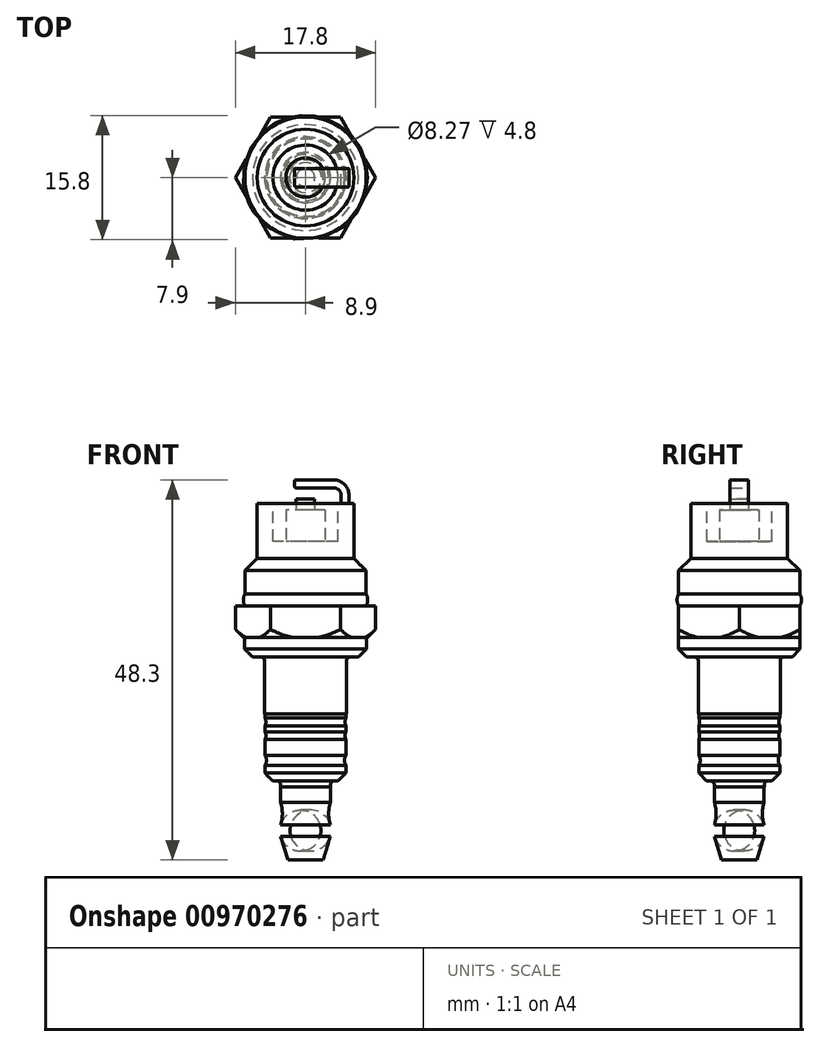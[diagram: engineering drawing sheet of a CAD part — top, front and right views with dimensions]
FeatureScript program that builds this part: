
annotation { "Feature Type Name" : "Feature", "Feature Type Description" : "" }
export const myFeature = defineFeature(function(context is Context, id is Id, definition is map)
    precondition{}
    {
        {
            var Q0;
            Q0=qCreatedBy(makeId("Front.planeOp"),FACE);
            var sketch = newSketch(context, id + "F0", { "sketchPlane" : qUnion([Q0])});
            skLineSegment(sketch, "E0", {"start": v(0, 22.65) * mm, "end": v(0, -22.65) * mm});
            skLineSegment(sketch, "E1", {"start": v(0, -22.65) * mm, "end": v(2.25, -22.65) * mm});
            skLineSegment(sketch, "E2", {"start": v(2.25, -22.65) * mm, "end": v(3.15, -19.65) * mm});
            skLineSegment(sketch, "E3", {"start": v(3.15, -18.15) * mm, "end": v(3.15, -15.35) * mm, "construction": true});
            skLineSegment(sketch, "E4", {"start": v(6.14, 22.65) * mm, "end": v(6.14, 15.65) * mm});
            skLineSegment(sketch, "E5", {"start": v(6.14, 15.65) * mm, "end": v(7.7, 14.15) * mm});
            skLineSegment(sketch, "E6", {"start": v(7.7, 14.15) * mm, "end": v(7.7, 11.15) * mm});
            skLineSegment(sketch, "E7", {"start": v(7.7, 11.15) * mm, "end": v(7.7, 9.65) * mm, "construction": true});
            skLineSegment(sketch, "E8", {"start": v(7.7, 9.65) * mm, "end": v(8.9, 9.65) * mm});
            skLineSegment(sketch, "E9", {"start": v(8.9, 9.65) * mm, "end": v(8.9, 5.65) * mm});
            skLineSegment(sketch, "E10", {"start": v(8.9, 5.65) * mm, "end": v(7.73, 5.65) * mm});
            skLineSegment(sketch, "E11", {"start": v(7.73, 5.65) * mm, "end": v(7.73, 3.15) * mm});
            skLineSegment(sketch, "E12", {"start": v(7.73, 3.15) * mm, "end": v(5.2, 3.15) * mm});
            skLineSegment(sketch, "E13", {"start": v(7.73, -1275.75) * mm, "end": v(7.53, -1275.75) * mm});
            skLineSegment(sketch, "E14", {"start": v(7.53, -408.95) * mm, "end": v(7.53, -1275.75) * mm});
            skLineSegment(sketch, "E15", {"start": v(7.53, -408.95) * mm, "end": v(7.73, -408.95) * mm});
            skLineSegment(sketch, "E16", {"start": v(7.73, -408.95) * mm, "end": v(7.73, -408.95) * mm});
            skLineSegment(sketch, "E17", {"start": v(5.2, -4.1) * mm, "end": v(5.15, -4.1) * mm});
            skLineSegment(sketch, "E18", {"start": v(5.15, -4.1) * mm, "end": v(5.15, -4.6) * mm});
            skLineSegment(sketch, "E19", {"start": v(5.15, -12.6) * mm, "end": v(3.18, -12.6) * mm});
            skLineSegment(sketch, "E20", {"start": v(3.18, -12.6) * mm, "end": v(3.18, -13.35) * mm});
            skLineSegment(sketch, "E21", {"start": v(3.18, -13.35) * mm, "end": v(3.15, -13.35) * mm});
            skLineSegment(sketch, "E22", {"start": v(3.15, -13.35) * mm, "end": v(3.15, -15.35) * mm});
            skLineSegment(sketch, "E23", {"start": v(6.14, 22.65) * mm, "end": v(4.14, 22.65) * mm});
            skLineSegment(sketch, "E24", {"start": v(4.14, 22.65) * mm, "end": v(4.14, 17.85) * mm});
            skLineSegment(sketch, "E25", {"start": v(4.14, 17.85) * mm, "end": v(0, 17.85) * mm});
            skArc(sketch, "E26", {"start": v(7.7, 9.65) * mm, "mid": v(7.9, 10.4) * mm, "end": v(7.7, 11.15) * mm});
            skPoint(sketch, "E27", {"position": v(3.15, -18.15) * mm});
            skArc(sketch, "E28", {"start": v(3.15, -19.65) * mm, "mid": v(3.26, -18.9) * mm, "end": v(3.15, -18.15) * mm});
            skArc(sketch, "E29", {"start": v(3.15, -15.35) * mm, "mid": v(2.94, -16.75) * mm, "end": v(3.15, -18.15) * mm});
            skLineSegment(sketch, "E30", {"start": v(5.2, -4.1) * mm, "end": v(5.2, 3.15) * mm});
            skLineSegment(sketch, "E31", {"start": v(5.15, -10.6) * mm, "end": v(5.15, -12.6) * mm});
            skLineSegment(sketch, "E32", {"start": v(5.15, -9.35) * mm, "end": v(5.15, -10.6) * mm, "construction": true});
            skLineSegment(sketch, "E33", {"start": v(5.15, -7.35) * mm, "end": v(5.15, -9.35) * mm});
            skLineSegment(sketch, "E34", {"start": v(5.15, -6.35) * mm, "end": v(5.15, -7.35) * mm, "construction": true});
            skLineSegment(sketch, "E35", {"start": v(5.15, -5.6) * mm, "end": v(5.15, -6.35) * mm});
            skLineSegment(sketch, "E36", {"start": v(5.15, -4.6) * mm, "end": v(5.15, -5.6) * mm, "construction": true});
            skArc(sketch, "E37", {"start": v(5.15, -9.35) * mm, "mid": v(4.96, -9.98) * mm, "end": v(5.15, -10.6) * mm});
            skArc(sketch, "E38", {"start": v(5.15, -4.6) * mm, "mid": v(5.03, -5.1) * mm, "end": v(5.15, -5.6) * mm});
            skArc(sketch, "E39", {"start": v(5.15, -6.35) * mm, "mid": v(5.03, -6.85) * mm, "end": v(5.15, -7.35) * mm});
            skSolve(sketch);
        }
        {
            var Q0;
            {var subQ1=sQuery(id+"F0.wireOp",EDGE,"E1");Q0=makeQuery(id+"F0.imprint","IMPRINT",FACE,{"disambiguationData":[TD([[makeQuery(id+"F0.imprint","IMPRINT",EDGE,{"derivedFrom":subQ1}),1.0]])]});}
            var Q1;
            Q1=sQuery(id+"F0.wireOp",EDGE,"E0");
            revolve(context, id + "F1", {"entities" : qUnion([Q0]), "axis" : qUnion([Q1]), "revolveType" : RevolveType.FULL});
        }
        {
            var Q0;
            Q0=makeQuery(id+"F1.opRevolve","SWEPT_FACE",FACE,{"disambiguationData":[OSD([sQuery(id+"F0.wireOp",EDGE,"E8")])]});
            var sketch = newSketch(context, id + "F2", { "sketchPlane" : qUnion([Q0])});
            skCircle(sketch, "E40.cCircle", {"center": v(0, 0) * mm, "radius": 7.7 * mm, "construction": true});
            skLineSegment(sketch, "E40.0", {"start": v(-4.45, 7.7) * mm, "end": v(4.45, 7.7) * mm});
            skLineSegment(sketch, "E40.1", {"start": v(4.45, 7.7) * mm, "end": v(8.9, 0) * mm});
            skLineSegment(sketch, "E40.2", {"start": v(8.9, 0) * mm, "end": v(4.45, -7.7) * mm});
            skLineSegment(sketch, "E40.3", {"start": v(4.45, -7.7) * mm, "end": v(-4.45, -7.7) * mm});
            skLineSegment(sketch, "E40.4", {"start": v(-4.45, -7.7) * mm, "end": v(-8.9, 0) * mm});
            skLineSegment(sketch, "E40.5", {"start": v(-8.9, 0) * mm, "end": v(-4.45, 7.7) * mm});
            skPoint(sketch, "E40.0.midPoint", {"position": v(0, 7.7) * mm});
            skSolve(sketch);
        }
        {
            var Q0;
            {var subQ0=sQuery(id+"F2.wireOp",EDGE,"E40.5");Q0=makeQuery(id+"F2.imprint","IMPRINT",FACE,{"disambiguationData":[TD([[makeQuery(id+"F2.imprint","IMPRINT",EDGE,{"derivedFrom":subQ0}),1.0]])]});}
            var Q1;
            {var subQ0=sQuery(id+"F2.wireOp",EDGE,"E40.4");Q1=makeQuery(id+"F2.imprint","IMPRINT",FACE,{"disambiguationData":[TD([[makeQuery(id+"F2.imprint","IMPRINT",EDGE,{"derivedFrom":subQ0}),1.0]])]});}
            var Q2;
            {var subQ0=sQuery(id+"F2.wireOp",EDGE,"E40.3");Q2=makeQuery(id+"F2.imprint","IMPRINT",FACE,{"disambiguationData":[TD([[makeQuery(id+"F2.imprint","IMPRINT",EDGE,{"derivedFrom":subQ0}),1.0]])]});}
            var Q3;
            {var subQ0=sQuery(id+"F2.wireOp",EDGE,"E40.2");Q3=makeQuery(id+"F2.imprint","IMPRINT",FACE,{"disambiguationData":[TD([[makeQuery(id+"F2.imprint","IMPRINT",EDGE,{"derivedFrom":subQ0}),1.0]])]});}
            var Q4;
            {var subQ0=sQuery(id+"F2.wireOp",EDGE,"E40.1");Q4=makeQuery(id+"F2.imprint","IMPRINT",FACE,{"disambiguationData":[TD([[makeQuery(id+"F2.imprint","IMPRINT",EDGE,{"derivedFrom":subQ0}),1.0]])]});}
            var Q5;
            {var subQ0=sQuery(id+"F2.wireOp",EDGE,"E40.0");Q5=makeQuery(id+"F2.imprint","IMPRINT",FACE,{"disambiguationData":[TD([[makeQuery(id+"F2.imprint","IMPRINT",EDGE,{"derivedFrom":subQ0}),1.0]])]});}
            var Q6;
            Q6=makeQuery(id+"F1.opRevolve","SWEPT_FACE",FACE,{"disambiguationData":[OSD([sQuery(id+"F0.wireOp",EDGE,"E10")])]});
            extrude(context, id + "F3", {"entities" : qUnion([Q0, Q1, Q2, Q3, Q4, Q5]), "operationType" : NewBodyOperationType.REMOVE, "endBound" : BoundingType.UP_TO_SURFACE, "oppositeDirection" : true, "endBoundEntityFace" : qUnion([Q6]), "depth" : 25 * mm});
        }
        {
            var Q0;
            Q0=makeQuery(id+"F1.opRevolve","SWEPT_FACE",FACE,{"disambiguationData":[OSD([sQuery(id+"F0.wireOp",EDGE,"E25")])]});
            var sketch = newSketch(context, id + "F4", { "sketchPlane" : qUnion([Q0])});
            skCircle(sketch, "E41", {"center": v(0, 0) * mm, "radius": 2.5 * mm});
            skCircle(sketch, "E42", {"center": v(0, 0) * mm, "radius": 1.18 * mm});
            skSolve(sketch);
        }
        {
            var Q0;
            Q0=makeQuery(id+"F4.imprint","IMPRINT",FACE,{"disambiguationData":[TD([[makeQuery(id+"F4.imprint","IMPRINT",EDGE,{"derivedFrom":sQuery(id+"F4.wireOp",EDGE,"E41")}),1.0]])]});
            extrude(context, id + "F5", {"entities" : qUnion([Q0]), "operationType" : NewBodyOperationType.ADD, "depth" : 4 * mm});
        }
        {
            var Q0;
            Q0=makeQuery(id+"F5.boolean.opBoolean","SPLIT",FACE,{"disambiguationData":[TD([makeQuery(id+"F5.opExtrude","SWEPT_FACE",FACE,{"disambiguationData":[OSD([sQuery(id+"F4.wireOp",EDGE,"E42")])]})])],"derivedFrom":makeQuery(id+"F1.opRevolve","SWEPT_FACE",FACE,{"disambiguationData":[OSD([sQuery(id+"F0.wireOp",EDGE,"E25")])]})});
            extrude(context, id + "F6", {"entities" : qUnion([Q0]), "operationType" : NewBodyOperationType.ADD, "depth" : 5.35 * mm});
        }
        {
            var Q0;
            Q0=makeQuery(id+"F1.opRevolve","SWEPT_EDGE",EDGE,{"disambiguationData":[OSD([sQuery(id+"F0.wireOp",EDGE,"E11"),sQuery(id+"F0.wireOp",EDGE,"E12")])]});
            var Q1;
            Q1=makeQuery(id+"F1.opRevolve","SWEPT_EDGE",EDGE,{"disambiguationData":[OSD([sQuery(id+"F0.wireOp",EDGE,"E19"),sQuery(id+"F0.wireOp",EDGE,"E31")])]});
            chamfer(context, id + "F7", {"entities" : qUnion([Q0, Q1]), "width" : 1 * mm, "tangentPropagation" : true});
        }
        {
            var Q0;
            Q0=qCreatedBy(makeId("Front.planeOp"),FACE);
            var sketch = newSketch(context, id + "F8", { "sketchPlane" : qUnion([Q0])});
            skLineSegment(sketch, "E43.0", {"start": v(8.9, 5.65) * mm, "end": v(7.9, 5.65) * mm});
            skLineSegment(sketch, "E43.1", {"start": v(8.9, 5.65) * mm, "end": v(8.9, 6.65) * mm});
            skLineSegment(sketch, "E44", {"start": v(7.9, 5.65) * mm, "end": v(8.9, 6.65) * mm});
            skPoint(sketch, "E45.orphan", {"position": v(8.9, 9.65) * mm});
            skPoint(sketch, "E46.orphan", {"position": v(6.93, 5.65) * mm});
            skSolve(sketch);
        }
        {
            var Q0;
            Q0=makeQuery(id+"F8.imprint","IMPRINT",FACE,{"disambiguationData":[TD([[makeQuery(id+"F8.imprint","IMPRINT",EDGE,{"derivedFrom":sQuery(id+"F8.wireOp",EDGE,"E43.0")}),-1.0]])]});
            var Q1;
            Q1=sQuery(id+"F0.wireOp",EDGE,"E0");
            revolve(context, id + "F9", {"operationType" : NewBodyOperationType.REMOVE, "entities" : qUnion([Q0]), "axis" : qUnion([Q1]), "revolveType" : RevolveType.FULL, "oppositeDirection" : true});
        }
        {
            var Q0;
            Q0=qCreatedBy(makeId("Front.planeOp"),FACE);
            var sketch = newSketch(context, id + "F10", { "sketchPlane" : qUnion([Q0])});
            skLineSegment(sketch, "E47", {"start": v(-1.36, 25.65) * mm, "end": v(5.54, 25.65) * mm});
            skLineSegment(sketch, "E48", {"start": v(5.54, 25.65) * mm, "end": v(5.54, 22.65) * mm});
            skLineSegment(sketch, "E49", {"start": v(5.54, 22.65) * mm, "end": v(4.54, 22.65) * mm});
            skLineSegment(sketch, "E50.0", {"start": v(4.54, 24.65) * mm, "end": v(4.54, 22.65) * mm});
            skLineSegment(sketch, "E50.1", {"start": v(-1.36, 24.65) * mm, "end": v(4.54, 24.65) * mm});
            skLineSegment(sketch, "E51", {"start": v(-1.36, 25.65) * mm, "end": v(-1.36, 24.65) * mm});
            skSolve(sketch);
        }
        {
            var Q0;
            Q0=makeQuery(id+"F10.imprint","IMPRINT",FACE,{"disambiguationData":[TD([[makeQuery(id+"F10.imprint","IMPRINT",EDGE,{"derivedFrom":sQuery(id+"F10.wireOp",EDGE,"E47")}),-1.0]])]});
            extrude(context, id + "F11", {"entities" : qUnion([Q0]), "operationType" : NewBodyOperationType.ADD, "endBound" : BoundingType.SYMMETRIC, "depth" : 2.35 * mm});
        }
        {
            var Q0;
            Q0=makeQuery(id+"F11.opExtrude","SWEPT_EDGE",EDGE,{"disambiguationData":[OSD([sQuery(id+"F10.wireOp",EDGE,"E50.0"),sQuery(id+"F10.wireOp",EDGE,"E50.1")])]});
            fillet(context, id + "F12", {"entities" : qUnion([Q0]), "radius" : 1 * mm, "tangentPropagation" : true, "conicFillet" : false});
        }
        {
            var Q0;
            Q0=makeQuery(id+"F11.opExtrude","SWEPT_EDGE",EDGE,{"disambiguationData":[OSD([sQuery(id+"F10.wireOp",EDGE,"E47"),sQuery(id+"F10.wireOp",EDGE,"E48")])]});
            fillet(context, id + "F13", {"entities" : qUnion([Q0]), "radius" : 2 * mm, "tangentPropagation" : true, "conicFillet" : false});
        }
        {
            var Q0;
            Q0=makeQuery(id+"F11.opExtrude","CAP_FACE",FACE,{"disambiguationData":[OSD([sQuery(id+"F10.wireOp",EDGE,"E47"),sQuery(id+"F10.wireOp",EDGE,"E48"),sQuery(id+"F10.wireOp",EDGE,"E49"),sQuery(id+"F10.wireOp",EDGE,"E50.0"),sQuery(id+"F10.wireOp",EDGE,"E50.1"),sQuery(id+"F10.wireOp",EDGE,"E51")])],"isStart":false});
            var Q1;
            Q1=makeQuery(id+"F11.opExtrude","SWEPT_FACE",FACE,{"disambiguationData":[OSD([sQuery(id+"F10.wireOp",EDGE,"E51")])]});
            var Q2;
            Q2=makeQuery(id+"F11.opExtrude","CAP_FACE",FACE,{"disambiguationData":[OSD([sQuery(id+"F10.wireOp",EDGE,"E47"),sQuery(id+"F10.wireOp",EDGE,"E48"),sQuery(id+"F10.wireOp",EDGE,"E49"),sQuery(id+"F10.wireOp",EDGE,"E50.0"),sQuery(id+"F10.wireOp",EDGE,"E50.1"),sQuery(id+"F10.wireOp",EDGE,"E51")])],"isStart":true});
            fillet(context, id + "F14", {"entities" : qUnion([Q0, Q1, Q2]), "radius" : 0.1 * mm, "tangentPropagation" : true, "conicFillet" : false});
        }
        {
            var Q0;
            Q0=makeQuery(id+"F1.opRevolve","SWEPT_EDGE",EDGE,{"disambiguationData":[OSD([sQuery(id+"F0.wireOp",EDGE,"E12"),sQuery(id+"F0.wireOp",EDGE,"E30")])]});
            var Q1;
            Q1=makeQuery(id+"F1.opRevolve","SWEPT_EDGE",EDGE,{"disambiguationData":[OSD([sQuery(id+"F0.wireOp",EDGE,"E19"),sQuery(id+"F0.wireOp",EDGE,"E20")])]});
            fillet(context, id + "F15", {"entities" : qUnion([Q0, Q1]), "radius" : 0.5 * mm, "tangentPropagation" : true, "conicFillet" : false});
        }
    });
